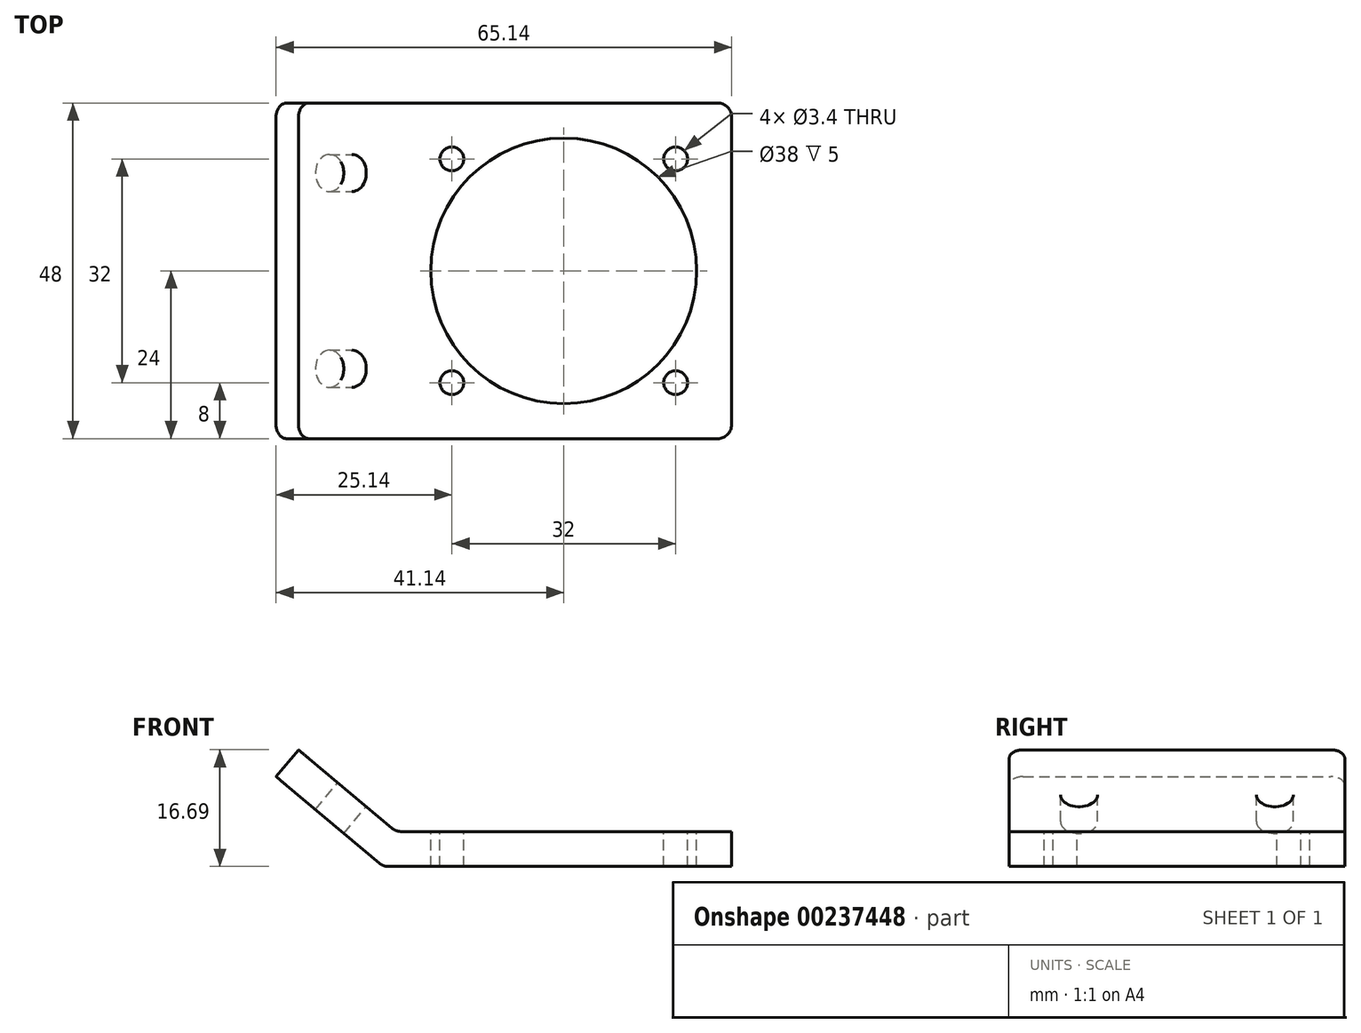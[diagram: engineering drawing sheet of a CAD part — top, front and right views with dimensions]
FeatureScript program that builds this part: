
annotation { "Feature Type Name" : "Feature", "Feature Type Description" : "" }
export const myFeature = defineFeature(function(context is Context, id is Id, definition is map)
    precondition{}
    {
        {
            var Q0;
            Q0=qCreatedBy(makeId("Top.planeOp"),FACE);
            var sketch = newSketch(context, id + "F0", { "sketchPlane" : qUnion([Q0])});
            skLineSegment(sketch, "E0.bottom", {"start": v(-20, 5) * mm, "end": v(-1.82, 5) * mm});
            skLineSegment(sketch, "E0.top", {"start": v(-20, 0) * mm, "end": v(0, 0) * mm});
            skLineSegment(sketch, "E0.left", {"start": v(-20, 5) * mm, "end": v(-20, 0) * mm});
            skLineSegment(sketch, "E1", {"start": v(0, 0) * mm, "end": v(38.16, 32.02) * mm});
            skLineSegment(sketch, "E2", {"start": v(38.16, 32.02) * mm, "end": v(34.95, 35.85) * mm});
            skLineSegment(sketch, "E3", {"start": v(34.95, 35.85) * mm, "end": v(-1.82, 5) * mm});
            skSolve(sketch);
        }
        {
            var Q0;
            Q0 = qSketchRegion(id + "F0", true);
            extrude(context, id + "F1", {"entities" : qUnion([Q0]), "depth" : 48 * mm});
        }
        {
            var Q0;
            Q0=makeQuery(id+"F1.opExtrude","SWEPT_FACE",FACE,{"disambiguationData":[OSD([sQuery(id+"F0.wireOp",EDGE,"E0.bottom")])]});
            var sketch = newSketch(context, id + "F2", { "sketchPlane" : qUnion([Q0])});
            skCircle(sketch, "E4", {"center": v(10, 38) * mm, "radius": 2.65 * mm});
            skCircle(sketch, "E5", {"center": v(10, 10) * mm, "radius": 2.65 * mm});
            skSolve(sketch);
        }
        {
            var Q0;
            Q0=makeQuery(id+"F2.imprint","IMPRINT",FACE,{"disambiguationData":[TD([[makeQuery(id+"F2.imprint","IMPRINT",EDGE,{"derivedFrom":sQuery(id+"F2.wireOp",EDGE,"E5")}),1.0]])]});
            var Q1;
            Q1=makeQuery(id+"F2.imprint","IMPRINT",FACE,{"disambiguationData":[TD([[makeQuery(id+"F2.imprint","IMPRINT",EDGE,{"derivedFrom":sQuery(id+"F2.wireOp",EDGE,"E4")}),1.0]])]});
            var Q2;
            Q2=makeQuery(id+"F1.opExtrude","SWEPT_FACE",FACE,{"disambiguationData":[OSD([sQuery(id+"F0.wireOp",EDGE,"E0.top")])]});
            extrude(context, id + "F3", {"entities" : qUnion([Q0, Q1]), "operationType" : NewBodyOperationType.REMOVE, "endBound" : BoundingType.UP_TO_SURFACE, "oppositeDirection" : true, "endBoundEntityFace" : qUnion([Q2]), "depth" : 25 * mm});
        }
        {
            var Q0;
            Q0=makeQuery(id+"F1.opExtrude","SWEPT_FACE",FACE,{"disambiguationData":[OSD([sQuery(id+"F0.wireOp",EDGE,"E3")])]});
            var sketch = newSketch(context, id + "F4", { "sketchPlane" : qUnion([Q0])});
            skCircle(sketch, "E6", {"center": v(-25.82, 24) * mm, "radius": 19 * mm});
            skCircle(sketch, "E7", {"center": v(-9.82, 8) * mm, "radius": 1.7 * mm});
            skCircle(sketch, "E8", {"center": v(-9.82, 40) * mm, "radius": 1.7 * mm});
            skCircle(sketch, "E9", {"center": v(-41.82, 8) * mm, "radius": 1.7 * mm});
            skCircle(sketch, "E10", {"center": v(-41.82, 40) * mm, "radius": 1.7 * mm});
            skSolve(sketch);
        }
        {
            var Q0;
            Q0=makeQuery(id+"F4.imprint","IMPRINT",FACE,{"disambiguationData":[TD([[makeQuery(id+"F4.imprint","IMPRINT",EDGE,{"derivedFrom":sQuery(id+"F4.wireOp",EDGE,"E6")}),1.0]])]});
            var Q1;
            Q1=makeQuery(id+"F4.imprint","IMPRINT",FACE,{"disambiguationData":[TD([[makeQuery(id+"F4.imprint","IMPRINT",EDGE,{"derivedFrom":sQuery(id+"F4.wireOp",EDGE,"E8")}),1.0]])]});
            var Q2;
            Q2=makeQuery(id+"F4.imprint","IMPRINT",FACE,{"disambiguationData":[TD([[makeQuery(id+"F4.imprint","IMPRINT",EDGE,{"derivedFrom":sQuery(id+"F4.wireOp",EDGE,"E7")}),1.0]])]});
            var Q3;
            Q3=makeQuery(id+"F4.imprint","IMPRINT",FACE,{"disambiguationData":[TD([[makeQuery(id+"F4.imprint","IMPRINT",EDGE,{"derivedFrom":sQuery(id+"F4.wireOp",EDGE,"E9")}),1.0]])]});
            var Q4;
            Q4=makeQuery(id+"F4.imprint","IMPRINT",FACE,{"disambiguationData":[TD([[makeQuery(id+"F4.imprint","IMPRINT",EDGE,{"derivedFrom":sQuery(id+"F4.wireOp",EDGE,"E10")}),1.0]])]});
            var Q5;
            Q5=makeQuery(id+"F1.opExtrude","SWEPT_FACE",FACE,{"disambiguationData":[OSD([sQuery(id+"F0.wireOp",EDGE,"E1")])]});
            extrude(context, id + "F5", {"entities" : qUnion([Q0, Q1, Q2, Q3, Q4]), "operationType" : NewBodyOperationType.REMOVE, "endBound" : BoundingType.UP_TO_SURFACE, "oppositeDirection" : true, "endBoundEntityFace" : qUnion([Q5]), "depth" : 25 * mm});
        }
        {
            var Q0;
            Q0=makeQuery(id+"F1.opExtrude","SWEPT_BODY",BODY,{"disambiguationData":[OSD([sQuery(id+"F0.wireOp",EDGE,"E0.bottom"),sQuery(id+"F0.wireOp",EDGE,"E0.top"),sQuery(id+"F0.wireOp",EDGE,"E0.left"),sQuery(id+"F0.wireOp",EDGE,"E1"),sQuery(id+"F0.wireOp",EDGE,"E2"),sQuery(id+"F0.wireOp",EDGE,"E3")])]});
            var Q1;
            Q1=makeQuery(id+"F1.opExtrude","SWEPT_EDGE",EDGE,{"disambiguationData":[OSD([sQuery(id+"F0.wireOp",EDGE,"E0.top"),sQuery(id+"F0.wireOp",EDGE,"E1")])]});
            transform(context, id + "F6", {"entities" : qUnion([Q0]), "transformType" : TransformType.ROTATION, "transformAxis" : qUnion([Q1]), "angle" : 40 * degree, "makeCopy" : false});
        }
        {
            var Q0;
            Q0=makeQuery(id+"F1.opExtrude","SWEPT_BODY",BODY,{"disambiguationData":[OSD([sQuery(id+"F0.wireOp",EDGE,"E0.bottom"),sQuery(id+"F0.wireOp",EDGE,"E0.top"),sQuery(id+"F0.wireOp",EDGE,"E0.left"),sQuery(id+"F0.wireOp",EDGE,"E1"),sQuery(id+"F0.wireOp",EDGE,"E2"),sQuery(id+"F0.wireOp",EDGE,"E3")])]});
            var Q1;
            Q1=makeQuery(id+"F1.opExtrude","CAP_EDGE",EDGE,{"disambiguationData":[OSD([sQuery(id+"F0.wireOp",EDGE,"E1")])],"isStart":true});
            transform(context, id + "F7", {"entities" : qUnion([Q0]), "transformType" : TransformType.ROTATION, "transformAxis" : qUnion([Q1]), "angle" : 90 * degree, "makeCopy" : false});
        }
        {
            var Q0;
            Q0=makeQuery(id+"F1.opExtrude","SWEPT_EDGE",EDGE,{"disambiguationData":[OSD([sQuery(id+"F0.wireOp",EDGE,"E0.bottom"),sQuery(id+"F0.wireOp",EDGE,"E3")])]});
            var Q1;
            Q1=makeQuery(id+"F1.opExtrude","SWEPT_EDGE",EDGE,{"disambiguationData":[OSD([sQuery(id+"F0.wireOp",EDGE,"E0.top"),sQuery(id+"F0.wireOp",EDGE,"E1")])]});
            var Q2;
            Q2=makeQuery(id+"F1.opExtrude","CAP_EDGE",EDGE,{"disambiguationData":[OSD([sQuery(id+"F0.wireOp",EDGE,"E0.left")])],"isStart":true});
            var Q3;
            Q3=makeQuery(id+"F1.opExtrude","CAP_EDGE",EDGE,{"disambiguationData":[OSD([sQuery(id+"F0.wireOp",EDGE,"E0.left")])],"isStart":false});
            var Q4;
            Q4=makeQuery(id+"F1.opExtrude","CAP_EDGE",EDGE,{"disambiguationData":[OSD([sQuery(id+"F0.wireOp",EDGE,"E2")])],"isStart":true});
            var Q5;
            Q5=makeQuery(id+"F1.opExtrude","CAP_EDGE",EDGE,{"disambiguationData":[OSD([sQuery(id+"F0.wireOp",EDGE,"E2")])],"isStart":false});
            fillet(context, id + "F8", {"entities" : qUnion([Q0, Q1, Q2, Q3, Q4, Q5]), "radius" : 2 * mm, "tangentPropagation" : true, "allowEdgeOverflow" : false});
        }
    });
